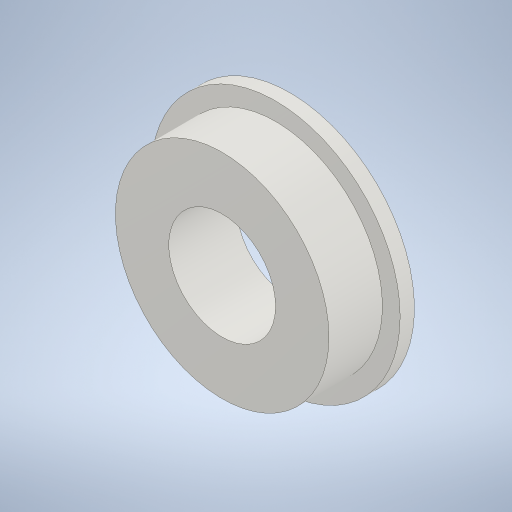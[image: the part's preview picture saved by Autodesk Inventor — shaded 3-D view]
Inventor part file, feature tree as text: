
AUTODESK INVENTOR PART (.ipt)
format: ipt  version: 2023 (Build 270158030, 158C)  size: 332,288 bytes
history: native  units: mm
features: projected_geometry x8, sketch x7, extrude x6, other x4, revolve x1, pattern_circular x1
ambient origin geometry x8: Origin, YZ Plane, XZ Plane, XY Plane, X Axis, Y Axis, Z Axis, Center Point
bodies: Body1 (feature_tree)
feature tree (27):
  other  "ソリッド1"
  extrude  "押し出し1"  Depth=14.0mm
  extrude  "押し出し2"  Depth=12.0mm
  other  "作業平面1"
  revolve  "回転1"
  pattern_circular  "円形状パターン1"  [2 undecoded]
  other  "作業平面2"
  other  "作業平面3"
  extrude  "押し出し3"  Depth=11.0mm
  extrude  "押し出し4"  Depth=6.0mm
  extrude  "押し出し5"  Depth=10.0mm
  extrude  "押し出し6"  Depth=7.0mm
  sketch  "スケッチ1"
  sketch  "スケッチ2"
  projected_geometry  "投影ループ1"
  sketch  "スケッチ3"
  projected_geometry  "投影ループ2"
  projected_geometry  "投影ループ3"
  sketch  "スケッチ4"
  projected_geometry  "投影ループ4"
  projected_geometry  "投影ループ5"
  sketch  "スケッチ5"
  projected_geometry  "投影ループ6"
  sketch  "スケッチ6"
  projected_geometry  "投影ループ7"
  sketch  "スケッチ7"
  projected_geometry  "投影ループ8"
note: 2 required parameter values undecoded (feature->parameter linkage not recoverable at this tier; creation-order binding heuristic only, values carry confidence <= 0.55)
